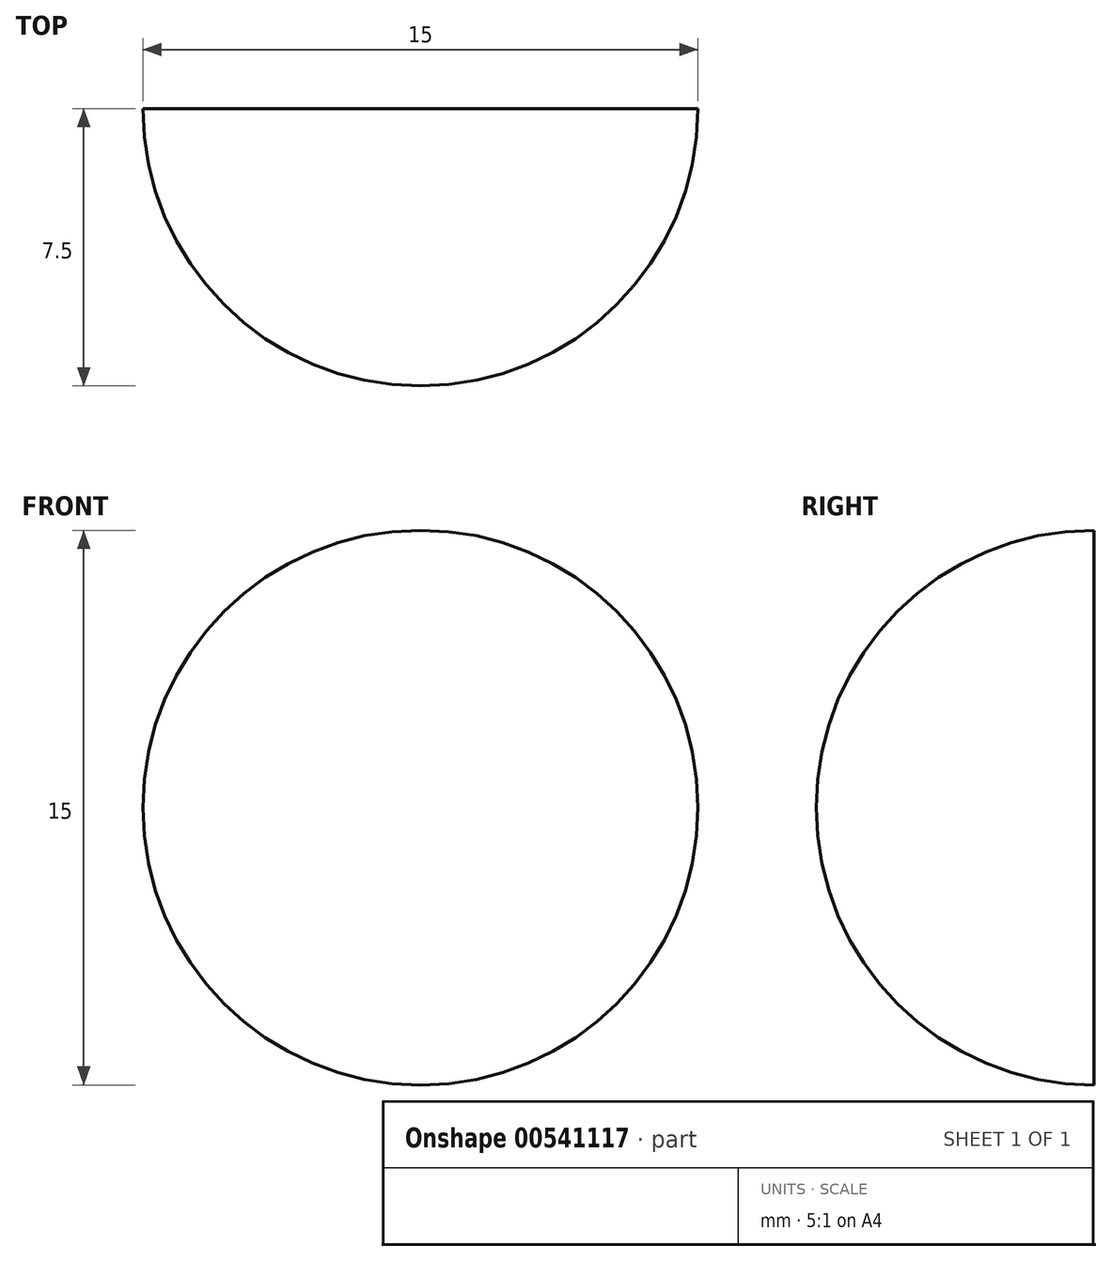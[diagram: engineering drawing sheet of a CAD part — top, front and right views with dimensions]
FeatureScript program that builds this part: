
annotation { "Feature Type Name" : "Feature", "Feature Type Description" : "" }
export const myFeature = defineFeature(function(context is Context, id is Id, definition is map)
    precondition{}
    {
        {
            var Q0;
            Q0=qCreatedBy(makeId("Front.planeOp"),FACE);
            var sketch = newSketch(context, id + "F0", { "sketchPlane" : qUnion([Q0])});
            skCircle(sketch, "E0", {"center": v(0, 0) * mm, "radius": 7.5 * mm});
            skLineSegment(sketch, "E1", {"start": v(0, 0) * mm, "end": v(0, 7.5) * mm});
            skLineSegment(sketch, "E2", {"start": v(0, 0) * mm, "end": v(0, -7.5) * mm});
            skSolve(sketch);
        }
        {
            var Q0;
            {var subQ0=sQuery(id+"F0.wireOp",EDGE,"E1");Q0=makeQuery(id+"F0.imprint","IMPRINT",FACE,{"disambiguationData":[TD([[makeQuery(id+"F0.imprint","IMPRINT",EDGE,{"derivedFrom":subQ0}),-1.0]])]});}
            var Q1;
            Q1=sQuery(id+"F0.wireOp",EDGE,"E1");
            revolve(context, id + "F1", {"entities" : qUnion([Q0]), "axis" : qUnion([Q1]), "revolveType" : RevolveType.ONE_DIRECTION, "oppositeDirection" : true, "angle" : 180 * degree});
        }
    });
